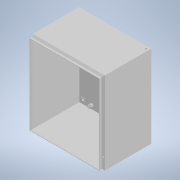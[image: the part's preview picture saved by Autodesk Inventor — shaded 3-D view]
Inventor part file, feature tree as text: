
AUTODESK INVENTOR PART (.ipt)
format: ipt  version: 2021 (Build 250183000, 183)  size: 541,184 bytes
history: native  units: mm
features: sketch x37, extrude x32, other x28, revolve x4, hole x1
ambient origin geometry x8: Origin, YZ Plane, XZ Plane, XY Plane, X Axis, Y Axis, Z Axis, Center Point
bodies: Solid1 (feature_tree)
feature tree (102):
  extrude  "Extrusion1"  Depth=225.65mm TaperAngle=0.0deg
  extrude  "Extrusion2"  Depth=350.0mm TaperAngle=0.0deg
  extrude  "Extrusion3"  Depth=400.0mm TaperAngle=0.0deg
  extrude  "Extrusion4"  Depth=18.0mm TaperAngle=0.0deg
  extrude  "Extrusion5"  Depth=18.0mm TaperAngle=0.0deg
  extrude  "Extrusion6"  Depth=18.0mm TaperAngle=0.0deg
  extrude  "Extrusion7"  Depth=18.0mm TaperAngle=0.0deg
  extrude  "Extrusion8"  Depth=16.0mm TaperAngle=0.0deg
  extrude  "Extrusion9"  Depth=16.0mm TaperAngle=0.0deg
  extrude  "Extrusion10"  Depth=8.0mm TaperAngle=0.0deg
  extrude  "Extrusion11"  Depth=8.0mm TaperAngle=0.0deg
  extrude  "Extrusion12"  Depth=8.0mm TaperAngle=0.0deg
  extrude  "Extrusion13"  Depth=400.0mm TaperAngle=0.0deg
  extrude  "Extrusion14"  Depth=400.0mm TaperAngle=0.0deg
  extrude  "Extrusion15"  TaperAngle=360.0deg  [1 undecoded]
  extrude  "Extrusion16"  Depth=2.5mm TaperAngle=0.0deg
  extrude  "Extrusion17"  TaperAngle=360.0deg  [1 undecoded]
  extrude  "Extrusion18"  TaperAngle=360.0deg  [1 undecoded]
  extrude  "Extrusion19"  TaperAngle=0.0deg  [1 undecoded]
  extrude  "Extrusion20"  [1 undecoded]
  extrude  "Extrusion21"  [1 undecoded]
  extrude  "Extrusion22"  [1 undecoded]
  extrude  "Extrusion23"  [1 undecoded]
  extrude  "Extrusion24"  [1 undecoded]
  extrude  "Extrusion25"  [1 undecoded]
  extrude  "Extrusion26"  [1 undecoded]
  extrude  "Extrusion27"  [1 undecoded]
  extrude  "Extrusion28"  [1 undecoded]
  hole  "Hole1"  [1 undecoded]
  revolve  "Revolution1"  [1 undecoded]
  revolve  "Revolution2"  [1 undecoded]
  extrude  "Extrusion29"  [1 undecoded]
  extrude  "Extrusion30"  [1 undecoded]
  revolve  "Revolution3"  [1 undecoded]
  extrude  "Extrusion31"  [1 undecoded]
  revolve  "Revolution4"  [1 undecoded]
  extrude  "Extrusion32"  [1 undecoded]
  other  "dummy_XY"
  other  "dummy_YZ"
  other  "dummy_ZX"
  other  "dummy_X"
  other  "dummy_Y"
  other  "dummy_Z"
  other  "dummy_Center"
  other  "s1_XY"
  other  "s1_YZ"
  other  "s1_ZX"
  other  "s1_X"
  other  "s1_Y"
  other  "s1_Z"
  other  "s1_Center"
  other  "s2_XY"
  other  "s2_YZ"
  other  "s2_ZX"
  other  "s2_X"
  other  "s2_Y"
  other  "s2_Z"
  other  "s2_Center"
  other  "to_plate_XY"
  other  "to_plate_YZ"
  other  "to_plate_ZX"
  other  "to_plate_X"
  other  "to_plate_Y"
  other  "to_plate_Z"
  other  "to_plate_Center"
  sketch  "Sketch_1"  dims[d0=225.65mm d1=0.0mm d2=225.65mm d3=0.0mm]
  sketch  "Sketch_2"  dims[d4=350.0mm d5=0.0mm d6=350.0mm d7=0.0mm]
  sketch  "Sketch_3"  dims[d8=400.0mm d9=0.0mm d10=400.0mm d11=0.0mm]
  sketch  "Sketch_4"  dims[d12=18.0mm d13=0.0mm d14=18.0mm d15=0.0mm]
  sketch  "Sketch_5"  dims[d16=18.0mm d17=0.0mm d18=18.0mm d19=0.0mm]
  sketch  "Sketch_6"  dims[d20=18.0mm d21=0.0mm d22=18.0mm d23=0.0mm]
  sketch  "Sketch_7"  dims[d24=18.0mm d25=0.0mm d26=18.0mm d27=0.0mm]
  sketch  "Sketch_8"  dims[d28=16.0mm d29=0.0mm d30=16.0mm d31=0.0mm]
  sketch  "Sketch_9"  dims[d32=16.0mm d33=0.0mm d34=16.0mm d35=0.0mm]
  sketch  "Sketch_10"  dims[d36=8.0mm d37=0.0mm d38=8.0mm d39=0.0mm]
  sketch  "Sketch_11"  dims[d40=8.0mm d41=0.0mm d42=8.0mm d43=0.0mm]
  sketch  "Sketch_16"  dims[d44=8.0mm d45=0.0mm d46=8.0mm d47=0.0mm]
  sketch  "Sketch_17"  dims[d48=350.0mm d49=0.0mm d50=400.0mm d51=0.0mm]
  sketch  "Sketch_18"  dims[d52=350.0mm d53=0.0mm d54=400.0mm d55=0.0mm]
  sketch  "Sketch_23"  dims[d56=8.7mm d57=6.0mm d58=4.0mm d59=2.0mm d60=90.0deg d61=4.0mm d62=0.0mm d63=360.0deg]
  sketch  "Sketch_24"  dims[d64=360.0deg d65=2.5mm d66=0.0mm]
  sketch  "Sketch_25"  dims[d67=2.5mm d68=0.0mm d69=360.0deg]
  sketch  "Sketch_26"  dims[d70=2.5mm d71=0.0mm d72=360.0deg]
  sketch  "Sketch_27"  dims[d73=2.5mm d74=0.0mm d75=0.0mm d76=0.0mm d77=0.0mm]
  sketch  "Sketch_28"
  sketch  "Sketch_29"
  sketch  "Sketch_30"
  sketch  "Sketch_31"
  sketch  "Sketch_32"
  sketch  "Sketch_33"
  sketch  "Sketch_34"
  sketch  "Sketch_49"
  sketch  "Sketch_50"
  sketch  "Sketch29"
  sketch  "Sketch_64"
  sketch  "Sketch_65"
  sketch  "Sketch_66"
  sketch  "Sketch_67"
  sketch  "Sketch_68"
  sketch  "Sketch_69"
  sketch  "Sketch_70"
  sketch  "Sketch_71"
note: 22 required parameter values undecoded (feature->parameter linkage not recoverable at this tier; creation-order binding heuristic only, values carry confidence <= 0.55)
